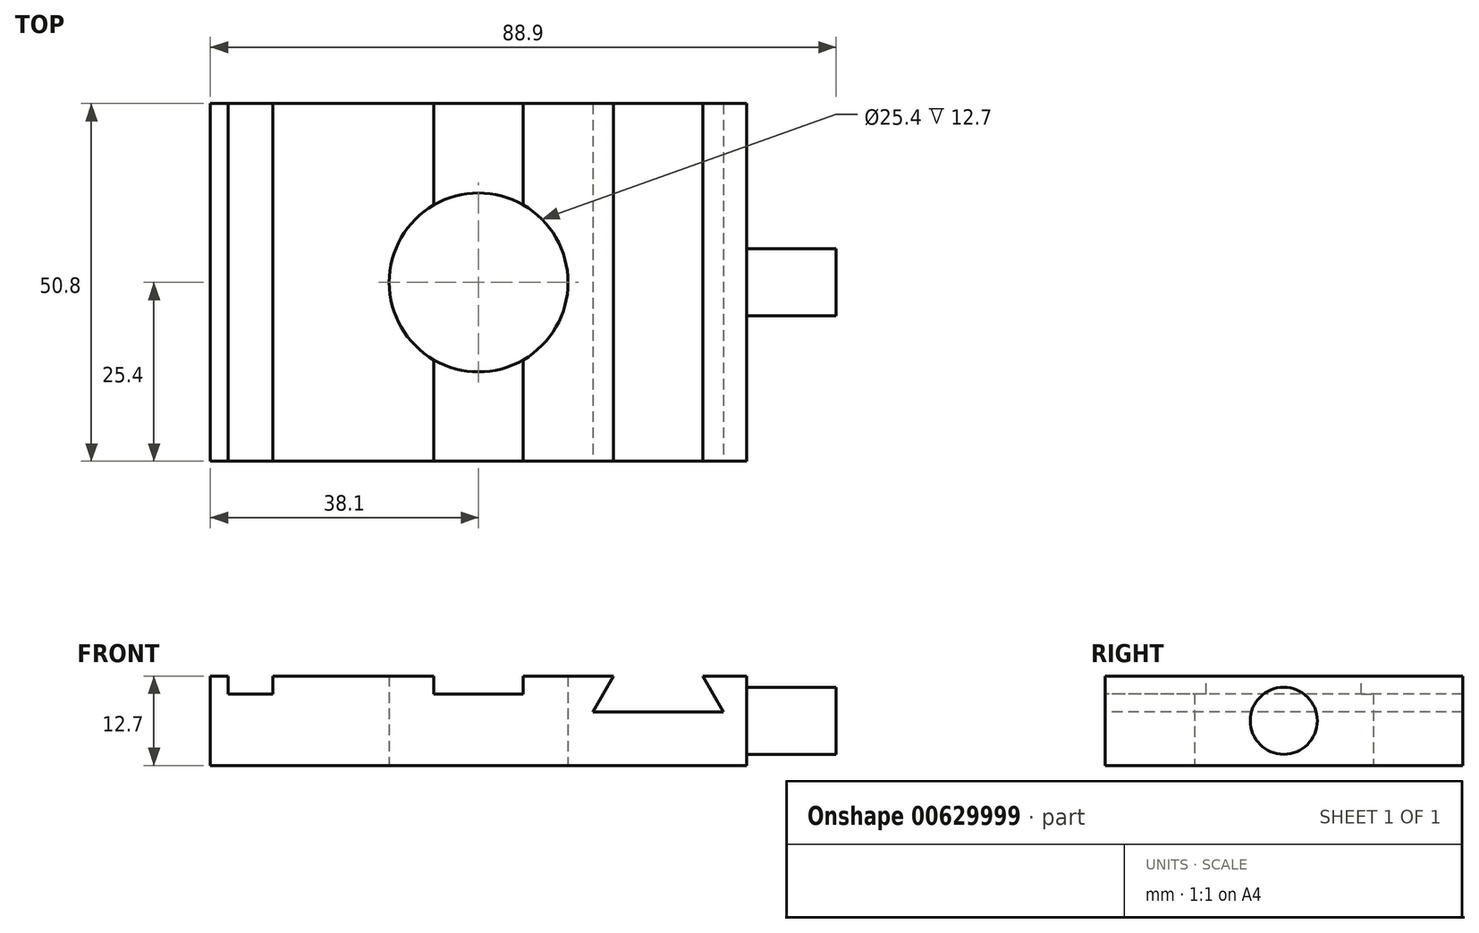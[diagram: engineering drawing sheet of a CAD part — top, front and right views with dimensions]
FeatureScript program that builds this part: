
annotation { "Feature Type Name" : "Feature", "Feature Type Description" : "" }
export const myFeature = defineFeature(function(context is Context, id is Id, definition is map)
    precondition{}
    {
        {
            var Q0;
            Q0=qCreatedBy(makeId("Top.planeOp"),FACE);
            var sketch = newSketch(context, id + "F0", { "sketchPlane" : qUnion([Q0])});
            skLineSegment(sketch, "E0.bottom", {"start": v(38.1, 25.4) * mm, "end": v(-38.1, 25.4) * mm});
            skLineSegment(sketch, "E0.top", {"start": v(38.1, -25.4) * mm, "end": v(-38.1, -25.4) * mm});
            skLineSegment(sketch, "E0.left", {"start": v(38.1, 25.4) * mm, "end": v(38.1, -25.4) * mm});
            skLineSegment(sketch, "E0.right", {"start": v(-38.1, 25.4) * mm, "end": v(-38.1, -25.4) * mm});
            skPoint(sketch, "E0.middle", {"position": v(0, 0) * mm});
            skCircle(sketch, "E1", {"center": v(0, 0) * mm, "radius": 12.7 * mm});
            skSolve(sketch);
        }
        {
            var Q0;
            Q0=makeQuery(id+"F0.imprint","IMPRINT",FACE,{"disambiguationData":[TD([[makeQuery(id+"F0.imprint","IMPRINT",EDGE,{"derivedFrom":sQuery(id+"F0.wireOp",EDGE,"E0.bottom")}),1.0]])]});
            extrude(context, id + "F1", {"entities" : qUnion([Q0]), "depth" : 12.7 * mm, "offsetDistance" : 25 * mm});
        }
        {
            var Q0;
            Q0=makeQuery(id+"F1.opExtrude","CAP_FACE",FACE,{"disambiguationData":[OSD([sQuery(id+"F0.wireOp",EDGE,"E0.bottom"),sQuery(id+"F0.wireOp",EDGE,"E0.top"),sQuery(id+"F0.wireOp",EDGE,"E0.left"),sQuery(id+"F0.wireOp",EDGE,"E0.right"),sQuery(id+"F0.wireOp",EDGE,"E1")])],"isStart":false});
            var sketch = newSketch(context, id + "F2", { "sketchPlane" : qUnion([Q0])});
            skLineSegment(sketch, "E2.bottom", {"start": v(-35.56, 25.4) * mm, "end": v(-29.2, 25.4) * mm});
            skLineSegment(sketch, "E2.top", {"start": v(-35.56, -25.4) * mm, "end": v(-29.2, -25.4) * mm});
            skLineSegment(sketch, "E2.left", {"start": v(-35.56, 25.4) * mm, "end": v(-35.56, -25.4) * mm});
            skLineSegment(sketch, "E2.right", {"start": v(-29.2, 25.4) * mm, "end": v(-29.2, -25.4) * mm});
            skPoint(sketch, "E3", {"position": v(0, 0) * mm});
            skLineSegment(sketch, "E4", {"start": v(-6.35, 25.4) * mm, "end": v(-6.35, -25.4) * mm});
            skLineSegment(sketch, "E5", {"start": v(-6.35, -25.4) * mm, "end": v(6.35, -25.4) * mm});
            skLineSegment(sketch, "E6", {"start": v(6.35, -25.4) * mm, "end": v(6.35, 25.4) * mm});
            skLineSegment(sketch, "E7", {"start": v(6.35, 25.4) * mm, "end": v(-6.35, 25.4) * mm});
            skLineSegment(sketch, "E8", {"start": v(0, 25.4) * mm, "end": v(0, -25.4) * mm, "construction": true});
            skSolve(sketch);
        }
        {
            var Q0;
            Q0=makeQuery(id+"F2.imprint","IMPRINT",FACE,{"disambiguationData":[TD([[makeQuery(id+"F2.imprint","IMPRINT",EDGE,{"derivedFrom":sQuery(id+"F2.wireOp",EDGE,"E2.bottom")}),1.0]])]});
            var Q1;
            {var subQ0=sQuery(id+"F2.wireOp",EDGE,"E7");Q1=makeQuery(id+"F2.imprint","IMPRINT",FACE,{"disambiguationData":[TD([[makeQuery(id+"F2.imprint","IMPRINT",EDGE,{"derivedFrom":subQ0}),1.0]])]});}
            var Q2;
            {var subQ0=sQuery(id+"F2.wireOp",EDGE,"E5");Q2=makeQuery(id+"F2.imprint","IMPRINT",FACE,{"disambiguationData":[TD([[makeQuery(id+"F2.imprint","IMPRINT",EDGE,{"derivedFrom":subQ0}),-1.0]])]});}
            extrude(context, id + "F3", {"entities" : qUnion([Q0, Q1, Q2]), "operationType" : NewBodyOperationType.REMOVE, "oppositeDirection" : true, "depth" : 2.54 * mm, "offsetDistance" : 25 * mm});
        }
        {
            var Q0;
            Q0=makeQuery(id+"F1.opExtrude","SWEPT_FACE",FACE,{"disambiguationData":[OSD([sQuery(id+"F0.wireOp",EDGE,"E0.top")])]});
            var sketch = newSketch(context, id + "F4", { "sketchPlane" : qUnion([Q0])});
            skLineSegment(sketch, "E9", {"start": v(19.15, 12.7) * mm, "end": v(16.22, 7.62) * mm});
            skLineSegment(sketch, "E10", {"start": v(16.22, 7.62) * mm, "end": v(34.78, 7.62) * mm});
            skLineSegment(sketch, "E11", {"start": v(34.78, 7.62) * mm, "end": v(31.85, 12.7) * mm});
            skLineSegment(sketch, "E12", {"start": v(31.85, 12.7) * mm, "end": v(19.15, 12.7) * mm});
            skLineSegment(sketch, "E13", {"start": v(25.5, 7.62) * mm, "end": v(25.5, 12.7) * mm, "construction": true});
            skSolve(sketch);
        }
        {
            var Q0;
            Q0=makeQuery(id+"F4.imprint","IMPRINT",FACE,{"disambiguationData":[TD([[makeQuery(id+"F4.imprint","IMPRINT",EDGE,{"derivedFrom":sQuery(id+"F4.wireOp",EDGE,"E9")}),1.0]])]});
            extrude(context, id + "F5", {"entities" : qUnion([Q0]), "operationType" : NewBodyOperationType.REMOVE, "endBound" : BoundingType.THROUGH_ALL, "oppositeDirection" : true, "depth" : 25 * mm, "offsetDistance" : 25 * mm});
        }
        {
            var Q0;
            Q0=makeQuery(id+"F1.opExtrude","SWEPT_FACE",FACE,{"disambiguationData":[OSD([sQuery(id+"F0.wireOp",EDGE,"E0.left")])]});
            var sketch = newSketch(context, id + "F6", { "sketchPlane" : qUnion([Q0])});
            skCircle(sketch, "E14", {"center": v(0, 6.35) * mm, "radius": 4.76 * mm});
            skPoint(sketch, "E14.centerSnap0", {"position": v(-25.4, 6.35) * mm});
            skPoint(sketch, "E14.centerSnap1", {"position": v(0, 12.7) * mm});
            skSolve(sketch);
        }
        {
            var Q0;
            Q0=makeQuery(id+"F6.imprint","IMPRINT",FACE,{"disambiguationData":[TD([[makeQuery(id+"F6.imprint","IMPRINT",EDGE,{"derivedFrom":sQuery(id+"F6.wireOp",EDGE,"E14")}),1.0]])]});
            extrude(context, id + "F7", {"entities" : qUnion([Q0]), "operationType" : NewBodyOperationType.ADD, "depth" : 12.7 * mm, "offsetDistance" : 25 * mm});
        }
    });
